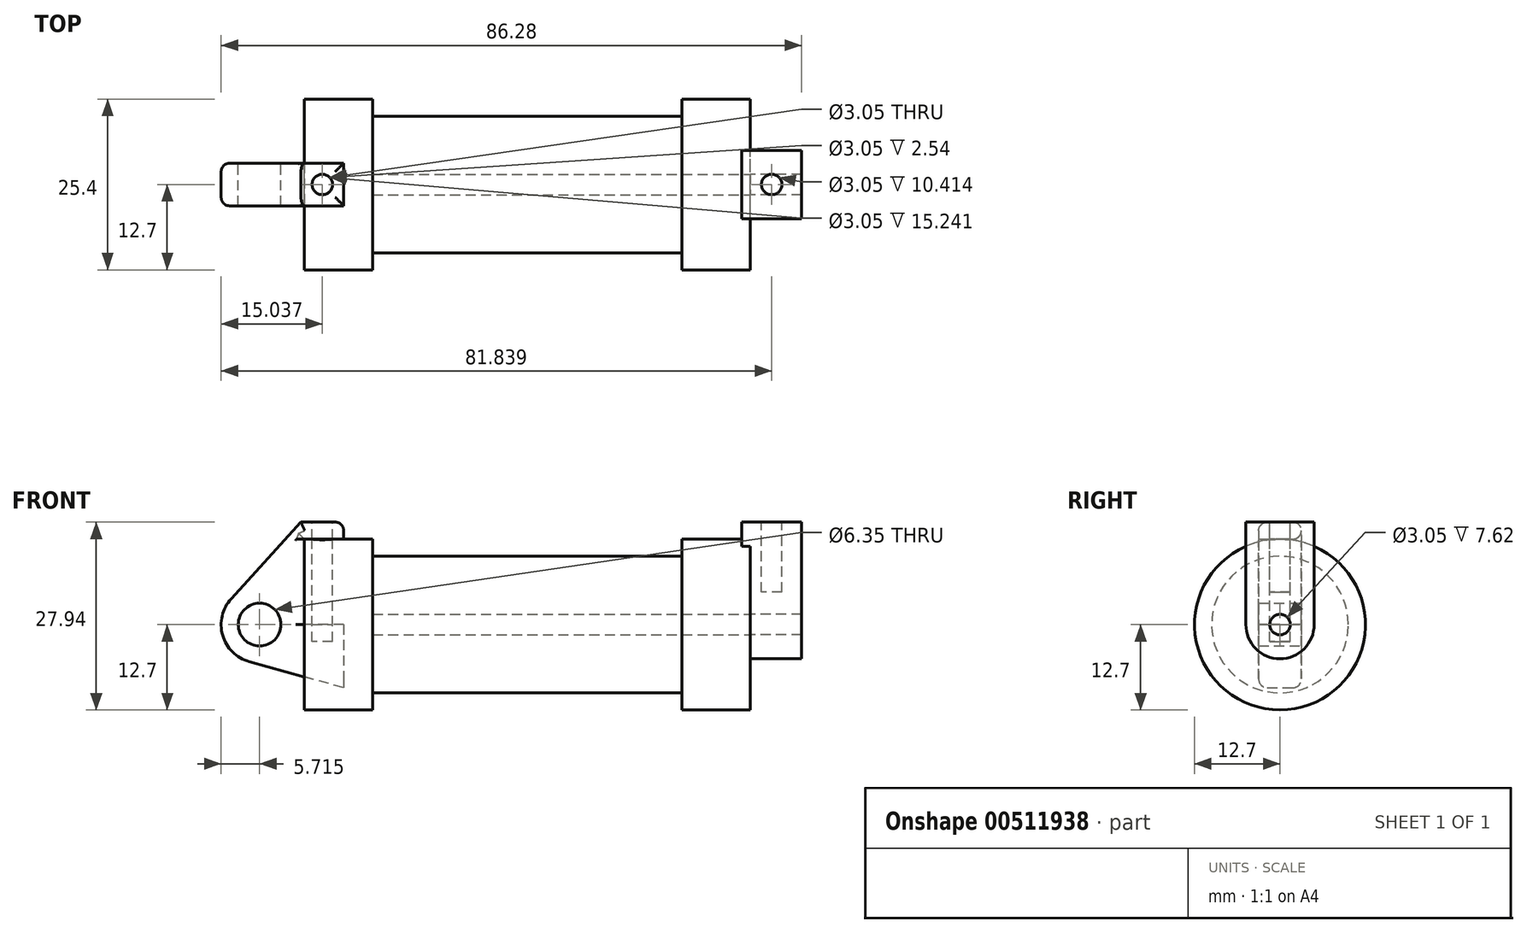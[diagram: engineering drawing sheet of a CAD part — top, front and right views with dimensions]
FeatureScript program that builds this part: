
annotation { "Feature Type Name" : "Feature", "Feature Type Description" : "" }
export const myFeature = defineFeature(function(context is Context, id is Id, definition is map)
    precondition{}
    {
        {
            var Q0;
            Q0=qCreatedBy(makeId("Front.planeOp"),FACE);
            var sketch = newSketch(context, id + "F0", { "sketchPlane" : qUnion([Q0])});
            skLineSegment(sketch, "E0", {"start": v(0, 0) * mm, "end": v(0, 12.7) * mm});
            skLineSegment(sketch, "E1", {"start": v(0, 12.7) * mm, "end": v(10.16, 12.7) * mm});
            skLineSegment(sketch, "E2", {"start": v(10.16, 12.7) * mm, "end": v(10.16, 10.16) * mm});
            skLineSegment(sketch, "E3", {"start": v(10.16, 10.16) * mm, "end": v(56.13, 10.16) * mm});
            skLineSegment(sketch, "E4", {"start": v(56.13, 10.16) * mm, "end": v(56.13, 12.7) * mm});
            skLineSegment(sketch, "E5", {"start": v(56.13, 12.7) * mm, "end": v(66.3, 12.7) * mm});
            skLineSegment(sketch, "E6", {"start": v(66.3, 12.7) * mm, "end": v(66.3, 0) * mm});
            skLineSegment(sketch, "E7", {"start": v(66.3, 0) * mm, "end": v(0, 0) * mm});
            skLineSegment(sketch, "E8", {"start": v(5.84, 15.24) * mm, "end": v(-0.5, 15.24) * mm});
            skLineSegment(sketch, "E9", {"start": v(-0.5, 15.24) * mm, "end": v(-10.88, 3.85) * mm});
            skLineSegment(sketch, "E10", {"start": v(0, 0) * mm, "end": v(-6.65, 0) * mm});
            skCircle(sketch, "E11", {"center": v(-6.65, 0) * mm, "radius": 5.72 * mm});
            skCircle(sketch, "E12", {"center": v(-6.65, 0) * mm, "radius": 3.18 * mm});
            skLineSegment(sketch, "E13", {"start": v(5.84, 15.24) * mm, "end": v(5.84, -9.4) * mm});
            skLineSegment(sketch, "E14", {"start": v(5.84, -9.4) * mm, "end": v(-8.18, -5.5) * mm});
            skSolve(sketch);
        }
        {
            var Q0;
            {var subQ0=sQuery(id+"F0.wireOp",EDGE,"E2");Q0=makeQuery(id+"F0.imprint","IMPRINT",FACE,{"disambiguationData":[TD([[makeQuery(id+"F0.imprint","IMPRINT",EDGE,{"derivedFrom":subQ0}),-1.0]])]});}
            var Q1;
            {var subQ0=sQuery(id+"F0.wireOp",EDGE,"E0");Q1=makeQuery(id+"F0.imprint","IMPRINT",FACE,{"disambiguationData":[TD([[makeQuery(id+"F0.imprint","IMPRINT",EDGE,{"derivedFrom":subQ0}),-1.0]])]});}
            var Q2;
            Q2=sQuery(id+"F0.wireOp",EDGE,"E7");
            revolve(context, id + "F1", {"entities" : qUnion([Q0, Q1]), "axis" : qUnion([Q2]), "revolveType" : RevolveType.FULL});
        }
        {
            var Q0;
            {var subQ1=sQuery(id+"F0.wireOp",EDGE,"E0");Q0=makeQuery(id+"F0.imprint","IMPRINT",FACE,{"disambiguationData":[TD([[makeQuery(id+"F0.imprint","IMPRINT",EDGE,{"derivedFrom":subQ1}),1.0]])]});}
            var Q1;
            {var subQ0=sQuery(id+"F0.wireOp",EDGE,"E14");Q1=makeQuery(id+"F0.imprint","IMPRINT",FACE,{"disambiguationData":[TD([[makeQuery(id+"F0.imprint","IMPRINT",EDGE,{"derivedFrom":subQ0}),-1.0]])]});}
            var Q2;
            {var subQ5=sQuery(id+"F0.wireOp",EDGE,"E12");Q2=makeQuery(id+"F0.imprint","IMPRINT",FACE,{"disambiguationData":[TD([[makeQuery(id+"F0.imprint","IMPRINT",EDGE,{"derivedFrom":subQ5}),-1.0]])]});}
            extrude(context, id + "F2", {"entities" : qUnion([Q0, Q1, Q2]), "endBound" : BoundingType.SYMMETRIC, "depth" : 6.35 * mm});
        }
        {
            var Q0;
            Q0=makeQuery(id+"F1.opRevolve","SWEPT_FACE",FACE,{"disambiguationData":[OSD([sQuery(id+"F0.wireOp",EDGE,"E6")])]});
            var sketch = newSketch(context, id + "F3", { "sketchPlane" : qUnion([Q0])});
            skCircle(sketch, "E15", {"center": v(0, 0) * mm, "radius": 1.52 * mm});
            skCircle(sketch, "E16", {"center": v(0, 0) * mm, "radius": 5.08 * mm});
            skLineSegment(sketch, "E17", {"start": v(-5.08, 0) * mm, "end": v(-5.08, 15.24) * mm});
            skLineSegment(sketch, "E18", {"start": v(-5.08, 15.24) * mm, "end": v(5.08, 15.24) * mm});
            skLineSegment(sketch, "E19", {"start": v(5.08, 15.24) * mm, "end": v(5.08, 0) * mm});
            skSolve(sketch);
        }
        {
            var Q0;
            {var subQ0=sQuery(id+"F3.wireOp",EDGE,"E18");Q0=makeQuery(id+"F3.imprint","IMPRINT",FACE,{"disambiguationData":[TD([[makeQuery(id+"F3.imprint","IMPRINT",EDGE,{"derivedFrom":subQ0}),-1.0]])]});}
            var Q1;
            {var subQ0=sQuery(id+"F3.wireOp",EDGE,"E17");var subQ1=sQuery(id+"F3.wireOp",EDGE,"E16");var subQ2=makeQuery(id+"F3.imprint","INTERSECT",VERTEX,{"derivedFrom":[subQ1,subQ0]});Q1=makeQuery(id+"F3.imprint","IMPRINT",FACE,{"disambiguationData":[TD([[makeQuery(id+"F3.imprint","IMPRINT",EDGE,{"disambiguationData":[TD([[subQ2,1.0]])],"derivedFrom":subQ1}),-1.0]])]});}
            var Q2;
            Q2=makeQuery(id+"F3.imprint","IMPRINT",FACE,{"disambiguationData":[TD([[makeQuery(id+"F3.imprint","IMPRINT",EDGE,{"derivedFrom":sQuery(id+"F3.wireOp",EDGE,"E15")}),-1.0]])]});
            extrude(context, id + "F4", {"entities" : qUnion([Q0, Q1, Q2]), "operationType" : NewBodyOperationType.ADD, "oppositeDirection" : true, "depth" : 1.27 * mm});
        }
        {
            var Q0;
            {var subQ0=sQuery(id+"F3.wireOp",EDGE,"E18");Q0=makeQuery(id+"F3.imprint","IMPRINT",FACE,{"disambiguationData":[TD([[makeQuery(id+"F3.imprint","IMPRINT",EDGE,{"derivedFrom":subQ0}),-1.0]])]});}
            var Q1;
            {var subQ0=sQuery(id+"F3.wireOp",EDGE,"E17");var subQ1=sQuery(id+"F3.wireOp",EDGE,"E16");var subQ2=makeQuery(id+"F3.imprint","INTERSECT",VERTEX,{"derivedFrom":[subQ1,subQ0]});Q1=makeQuery(id+"F3.imprint","IMPRINT",FACE,{"disambiguationData":[TD([[makeQuery(id+"F3.imprint","IMPRINT",EDGE,{"disambiguationData":[TD([[subQ2,1.0]])],"derivedFrom":subQ1}),-1.0]])]});}
            var Q2;
            Q2=makeQuery(id+"F3.imprint","IMPRINT",FACE,{"disambiguationData":[TD([[makeQuery(id+"F3.imprint","IMPRINT",EDGE,{"derivedFrom":sQuery(id+"F3.wireOp",EDGE,"E15")}),-1.0]])]});
            extrude(context, id + "F5", {"entities" : qUnion([Q0, Q1, Q2]), "operationType" : NewBodyOperationType.ADD, "depth" : 7.62 * mm});
        }
        {
            var Q0;
            Q0=makeQuery(id+"F3.imprint","IMPRINT",FACE,{"disambiguationData":[TD([[makeQuery(id+"F3.imprint","IMPRINT",EDGE,{"derivedFrom":sQuery(id+"F3.wireOp",EDGE,"E15")}),1.0]])]});
            var Q1;
            Q1=makeQuery(id+"F1.opRevolve","SWEPT_FACE",FACE,{"disambiguationData":[OSD([sQuery(id+"F0.wireOp",EDGE,"E2")])]});
            extrude(context, id + "F6", {"entities" : qUnion([Q0]), "endBound" : BoundingType.UP_TO_SURFACE, "oppositeDirection" : true, "endBoundEntityFace" : qUnion([Q1]), "depth" : 25.4 * mm});
        }
        {
            var Q0;
            {var subQ0=sQuery(id+"F3.wireOp",EDGE,"E18");Q0=makeQuery(id+"F5.boolean.opBoolean","MERGE",FACE,{"derivedFrom":[makeQuery(id+"F4.opExtrude","SWEPT_FACE",FACE,{"disambiguationData":[OSD([subQ0])]}),makeQuery(id+"F5.opExtrude","SWEPT_FACE",FACE,{"disambiguationData":[OSD([subQ0])]})]});}
            var sketch = newSketch(context, id + "F7", { "sketchPlane" : qUnion([Q0])});
            skCircle(sketch, "E20", {"center": v(69.47, 0) * mm, "radius": 1.52 * mm});
            skPoint(sketch, "E20.centerSnap0", {"position": v(73.91, 0) * mm});
            skPoint(sketch, "E20.centerSnap1", {"position": v(69.47, 5.08) * mm});
            skSolve(sketch);
        }
        {
            var Q0;
            Q0=makeQuery(id+"F7.imprint","IMPRINT",FACE,{"disambiguationData":[TD([[makeQuery(id+"F7.imprint","IMPRINT",EDGE,{"derivedFrom":sQuery(id+"F7.wireOp",EDGE,"E20")}),1.0]])]});
            var Q1;
            Q1=sQuery(id+"F7.wireOp",EDGE,"E20");
            extrude(context, id + "F8", {"entities" : qUnion([Q0]), "operationType" : NewBodyOperationType.REMOVE, "surfaceEntities" : qUnion([Q1]), "oppositeDirection" : true, "depth" : 10.4 * mm});
        }
        {
            var Q0;
            Q0=makeQuery(id+"F2.opExtrude","SWEPT_FACE",FACE,{"disambiguationData":[OSD([sQuery(id+"F0.wireOp",EDGE,"E8")])]});
            var sketch = newSketch(context, id + "F9", { "sketchPlane" : qUnion([Q0])});
            skCircle(sketch, "E21", {"center": v(2.67, 0) * mm, "radius": 1.52 * mm});
            skPoint(sketch, "E21.centerSnap0", {"position": v(2.67, -3.18) * mm});
            skPoint(sketch, "E21.centerSnap1", {"position": v(5.84, 0) * mm});
            skSolve(sketch);
        }
        {
            var Q0;
            Q0 = qSketchRegion(id + "F9", true);
            extrude(context, id + "F10", {"entities" : qUnion([Q0]), "operationType" : NewBodyOperationType.REMOVE, "oppositeDirection" : true, "depth" : 17.78 * mm});
        }
        {
            var Q0;
            Q0=makeQuery(id+"F1.opRevolve","SWEPT_EDGE",EDGE,{"disambiguationData":[OSD([sQuery(id+"F0.wireOp",EDGE,"E5"),sQuery(id+"F0.wireOp",EDGE,"E6")])]});
            var Q1;
            Q1=makeQuery(id+"F5.opExtrude","CAP_EDGE",EDGE,{"disambiguationData":[OSD([sQuery(id+"F3.wireOp",EDGE,"E19")])],"isStart":true});
            var Q2;
            Q2=makeQuery(id+"F5.opExtrude","CAP_EDGE",EDGE,{"disambiguationData":[OSD([sQuery(id+"F3.wireOp",EDGE,"E19")])],"isStart":false});
            var Q3;
            {var subQ0=sQuery(id+"F3.wireOp",EDGE,"E19");var subQ1=sQuery(id+"F3.wireOp",EDGE,"E18");Q3=makeQuery(id+"F5.boolean.opBoolean","MERGE",EDGE,{"derivedFrom":[makeQuery(id+"F4.opExtrude","SWEPT_EDGE",EDGE,{"disambiguationData":[OSD([subQ1,subQ0])]}),makeQuery(id+"F5.opExtrude","SWEPT_EDGE",EDGE,{"disambiguationData":[OSD([subQ1,subQ0])]})]});}
            var Q4;
            Q4=makeQuery(id+"F4.opExtrude","CAP_EDGE",EDGE,{"disambiguationData":[OSD([sQuery(id+"F3.wireOp",EDGE,"E19")])],"isStart":false});
            var Q5;
            Q5=makeQuery(id+"F5.opExtrude","CAP_EDGE",EDGE,{"disambiguationData":[OSD([sQuery(id+"F3.wireOp",EDGE,"E18")])],"isStart":false});
            var Q6;
            Q6=makeQuery(id+"F5.opExtrude","CAP_EDGE",EDGE,{"disambiguationData":[OSD([sQuery(id+"F3.wireOp",EDGE,"E17")])],"isStart":false});
            var Q7;
            {var subQ0=sQuery(id+"F3.wireOp",EDGE,"E17");Q7=makeQuery(id+"F5.boolean.opBoolean","MERGE",FACE,{"derivedFrom":[makeQuery(id+"F4.opExtrude","SWEPT_FACE",FACE,{"disambiguationData":[OSD([subQ0])]}),makeQuery(id+"F5.opExtrude","SWEPT_FACE",FACE,{"disambiguationData":[OSD([subQ0])]})]});}
            var Q8;
            Q8=makeQuery(id+"F5.opExtrude","CAP_EDGE",EDGE,{"disambiguationData":[OSD([sQuery(id+"F3.wireOp",EDGE,"E16")])],"isStart":true});
            var Q9;
            Q9=makeQuery(id+"F5.opExtrude","CAP_EDGE",EDGE,{"disambiguationData":[OSD([sQuery(id+"F3.wireOp",EDGE,"E16")])],"isStart":false});
            var Q10;
            Q10=makeQuery(id+"F1.opRevolve","SWEPT_EDGE",EDGE,{"disambiguationData":[OSD([sQuery(id+"F0.wireOp",EDGE,"E4"),sQuery(id+"F0.wireOp",EDGE,"E5")])]});
            var Q11;
            Q11=makeQuery(id+"F1.opRevolve","SWEPT_FACE",FACE,{"disambiguationData":[OSD([sQuery(id+"F0.wireOp",EDGE,"E3")])]});
            var Q12;
            Q12=makeQuery(id+"F1.opRevolve","SWEPT_FACE",FACE,{"disambiguationData":[OSD([sQuery(id+"F0.wireOp",EDGE,"E1")])]});
            var Q13;
            Q13=makeQuery(id+"F2.opExtrude","CAP_EDGE",EDGE,{"disambiguationData":[OSD([sQuery(id+"F0.wireOp",EDGE,"E9")])],"isStart":true});
            var Q14;
            Q14=makeQuery(id+"F2.opExtrude","CAP_EDGE",EDGE,{"disambiguationData":[OSD([sQuery(id+"F0.wireOp",EDGE,"E0")])],"isStart":true});
            var Q15;
            Q15=makeQuery(id+"F2.opExtrude","CAP_EDGE",EDGE,{"disambiguationData":[OSD([sQuery(id+"F0.wireOp",EDGE,"E1")])],"isStart":true});
            var Q16;
            Q16=makeQuery(id+"F2.opExtrude","SWEPT_EDGE",EDGE,{"disambiguationData":[OSD([sQuery(id+"F0.wireOp",EDGE,"E8"),sQuery(id+"F0.wireOp",EDGE,"E13")])]});
            var Q17;
            Q17=makeQuery(id+"F2.opExtrude","CAP_EDGE",EDGE,{"disambiguationData":[OSD([sQuery(id+"F0.wireOp",EDGE,"E9")])],"isStart":false});
            var Q18;
            Q18=makeQuery(id+"F2.opExtrude","CAP_EDGE",EDGE,{"disambiguationData":[OSD([sQuery(id+"F0.wireOp",EDGE,"E11")])],"isStart":false});
            var Q19;
            Q19=makeQuery(id+"F2.opExtrude","CAP_EDGE",EDGE,{"disambiguationData":[OSD([sQuery(id+"F0.wireOp",EDGE,"E8")])],"isStart":true});
            var Q20;
            Q20=makeQuery(id+"F2.opExtrude","CAP_EDGE",EDGE,{"disambiguationData":[OSD([sQuery(id+"F0.wireOp",EDGE,"E8")])],"isStart":false});
            var Q21;
            Q21=makeQuery(id+"F2.opExtrude","CAP_EDGE",EDGE,{"disambiguationData":[OSD([sQuery(id+"F0.wireOp",EDGE,"E0")])],"isStart":false});
            fillet(context, id + "F11", {"entities" : qUnion([Q0, Q1, Q2, Q3, Q4, Q5, Q6, Q7, Q8, Q9, Q10, Q11, Q12, Q13, Q14, Q15, Q16, Q17, Q18, Q19, Q20, Q21]), "radius" : 1.27 * mm, "tangentPropagation" : true, "allowEdgeOverflow" : false});
        }
    });
